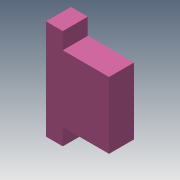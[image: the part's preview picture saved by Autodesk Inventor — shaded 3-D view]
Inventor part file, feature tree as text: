
AUTODESK INVENTOR PART (.ipt)
format: ipt  version: 2013 (Build 170138000, 138)  size: 81,408 bytes
history: native  units: mm
features: sketch x2, extrude x1
ambient origin geometry x8: Origin, YZ Plane, XZ Plane, XY Plane, X Axis, Y Axis, Z Axis, Center Point
bodies: Solid1 (feature_tree)
feature tree (3):
  sketch  "Sketch1"  dims[d6=37.9mm d7=55.0mm]
  extrude  "Extrusion1"  Depth=55.0mm
  sketch  "Sketch2"  dims[d9=60.0mm d10=10.0mm d11=10.0mm d12=15.0mm d13=0.0mm]
